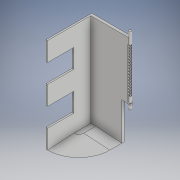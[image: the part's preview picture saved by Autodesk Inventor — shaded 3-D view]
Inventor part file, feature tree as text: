
AUTODESK INVENTOR PART (.ipt)
format: ipt  version: 2018 (Build 220112000, 112)  size: 841,728 bytes
history: native  units: mm
features: sketch x11, extrude x11, plane x5, other x3, pattern_circular x1, fillet x1, chamfer x1, mirror x1, projected_geometry x1
ambient origin geometry x8: Origin, YZ Plane, XZ Plane, XY Plane, X Axis, Y Axis, Z Axis, Center Point
bodies: Body1 (feature_tree)
feature tree (35):
  other  "Sólido1"
  sketch  "Boceto1"  dims[d0=100.0mm d1=145.0mm]
  extrude  "Extrusión2"  Depth=145.0mm
  extrude  "Extrusión3"  Depth=20.0mm
  plane  "Plano de trabajo1"
  extrude  "Extrusión4"  Depth=2.5mm TaperAngle=0.0deg
  extrude  "Extrusión5"  Depth=50.0mm TaperAngle=0.0deg
  extrude  "Extrusión6"  Depth=3.0mm
  sketch  "Boceto5"  dims[d29=0.0mm d31=50.0mm d32=0.0mm]
  extrude  "Extrusión8"  Depth=3.0mm
  extrude  "Extrusión9"  Depth=3.0mm
  plane  "Plano de trabajo2"
  other  "Bobina1"
  other  "Eje de trabajo1"
  pattern_circular  "Patrón circular1"  [2 undecoded]
  fillet  "Empalme1"  Radius=0.5mm
  chamfer  "Chaflán4"  Distance=2.0mm
  extrude  "Extrusión10"  Depth=2.0mm
  extrude  "Extrusión11"  Depth=2.0mm TaperAngle=360.0deg
  sketch  "Boceto10"  dims[d50=0.0mm d51=0.0mm]
  plane  "Plano de trabajo4"
  extrude  "Extrusión12"  Depth=2.0mm
  mirror  "Simetría1"
  plane  "Plano de trabajo5"
  plane  "Plano de trabajo6"
  extrude  "Extrusión13"  Depth=2.5mm TaperAngle=45.0deg
  sketch  "Boceto2"  dims[d2=4.0mm d12=20.0mm]
  sketch  "Boceto3"  dims[d25=2.5mm d26=0.0mm d27=50.0mm d28=0.0mm]
  projected_geometry  "Contorno proyectado1"
  sketch  "Boceto6"  dims[d33=2.5mm d34=0.0mm d38=3.0mm]
  sketch  "Boceto7"  dims[d42=12.5mm d43=0.0mm d44=3.0mm]
  sketch  "Boceto8"  dims[d45=3.0mm d48=12.5mm]
  sketch  "Boceto9"  dims[d49=12.5mm]
  sketch  "Boceto11"  dims[d52=4.0mm]
  sketch  "Boceto12"  dims[d53=15.0mm d54=0.0mm d56=2.0mm d57=0.5mm d58=2.0mm d59=0.5mm d60=10.0mm d61=100.0mm d62=200.0mm d63=0.0mm d64=90.0deg d65=90.0deg d66=0.0mm d67=0.0mm d68=50.0mm d69=360.0deg d71=47.5mm d75=2.5mm d76=40.0mm d77=45.0deg d78=4.0mm d79=10.0mm d80=0.0mm d81=4.0mm d82=8.0mm d83=0.0mm d85=50.0mm d86=90.0deg d88=1.5mm d89=1.5mm d90=2.499964mm d91=10.0mm d92=0.0mm d93=29.0mm d94=29.0mm d95=29.0mm d97=29.0mm d98=100.0mm d99=100.0mm d100=4.0mm d101=4.0mm d102=6.0mm d103=2.0mm d104=0.0mm]
note: 2 required parameter values undecoded (feature->parameter linkage not recoverable at this tier; creation-order binding heuristic only, values carry confidence <= 0.55)
